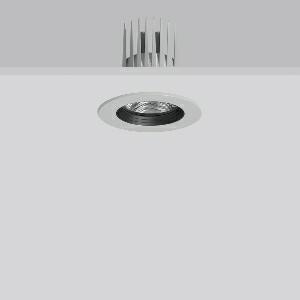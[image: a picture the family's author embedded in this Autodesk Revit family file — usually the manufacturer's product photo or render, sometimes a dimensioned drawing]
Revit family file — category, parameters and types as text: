
# Revit family: heledon_mini_e_901749_004_76_49e7
name_source: partatom
category: Lighting Fixtures
units: mm (PartAtom-declared; Revit-internal decimal feet)

## family parameters
Cut with Voids When Loaded = No
Host = Face
Light Source = No
Part Type = Normal
Room Calculation Point = No
Round Connector Dimension = Use Diameter
Shared = No

## types (1)
- HELEDON mini E (1 x LED Modul 930, 3500 lm, 3000)
    Apparent Load = 29 VA
    Approval mark = CE
    CIE Flux Codes = 99 100 100 100 100
    Color Rendering = 90
    Color Temperature = 3000
    Default Elevation = 1800 mm
    Description = Series: HELEDON mini
Round recessed downlight. Housing: die-cast aluminium, powder-coated. Black plastic ring and recessed LED to prevent glare from the side. Optical assembly with reflector made of MIRO-Silver with 98% total light reflection for outstanding efficiency - can be changed without tools. Best colour rendering index Ra>90. Suitable for Recessed ceiling mounting. Installation without tools thanks to spring fastening system. Including separate LED converter with connecting cable 600 mm.High quality converter without flickering and stroboscopic effect. Through-wiring box (5 pole) available as accessory. The following accessories can be mounted without use of tools: interchangeable lenses, decorative glasses, honeycomb louvre, clear and frosted diffusers, white interchangeable plastic ring. 
Colour: silver
Diameter: 124 mm
Height: 3 mm
Cut-out diameter: 114 mm
Recess height: 170 mm
Luminaire: recess height: 120 mm
Lamp: LED
Socket: without socket
Colour temperature: 3000K
Colour rendering index (CRI): 92
System power: 29 W
Rated luminous flux: 3500 lm
Luminous efficiency: 121 lm/W
Control gear: Converter, dimmable, DALI
Protection class: II
Type of protection: IP 20
    Height = 0 mm  [stored 0 ft]
    Lamp = 1 x LED Modul 930
    Lamp Light Flux = 3500 lm
    Lamp count = 1
    Length = 124 mm  [stored 0.406824 ft]
    Lifetime = 50000 h
    Luminous efficacy = 121 lm/W
    Manufacturer = RZB
    ModVariant = No
    Model = 901749.004.76
    Mounting Place = Ceiling
    Mounting Type = Recessed
    Number of Poles = 1
    OnlyDefault = Yes
    Power Factor = 1
    Product Name = HELEDON mini E
    Product group = Recessed downlights
    ProductGroupID = 402
    Protection Class = Protection class II
    Protection Degree = IP 20
    RLX_Detail_Level = 1
    RLX_Emergency_Light_Flux = 0 lm
    RLX_Emergency_Type = 0
    RLX_Emergency_Type_DB = No
    RlxData = <blob elided: 124445 chars, md5=6c1cf0f3>
    Socket = socket
    Standby Power = 0 W
    System Light Flux = 3500 lm
    System Power = 29 W
    Type Comments = Product without accessories
    Type Image = 901657.004.jpg
    URL = http://relux.com
    VarID = ---
    Voltage = 230 V
    Voltage Range = 220-240 V
    Weight = 0.00 kg
    Width = 0 mm  [stored 0 ft]

note: [stored X ft] marks values corroborated as IEEE doubles in the binary element streams (Revit-internal decimal feet)

## geometry (parser evidence)
native form markers: Blend x4, Sweep x9
no freeform markers — native parametric forms only
